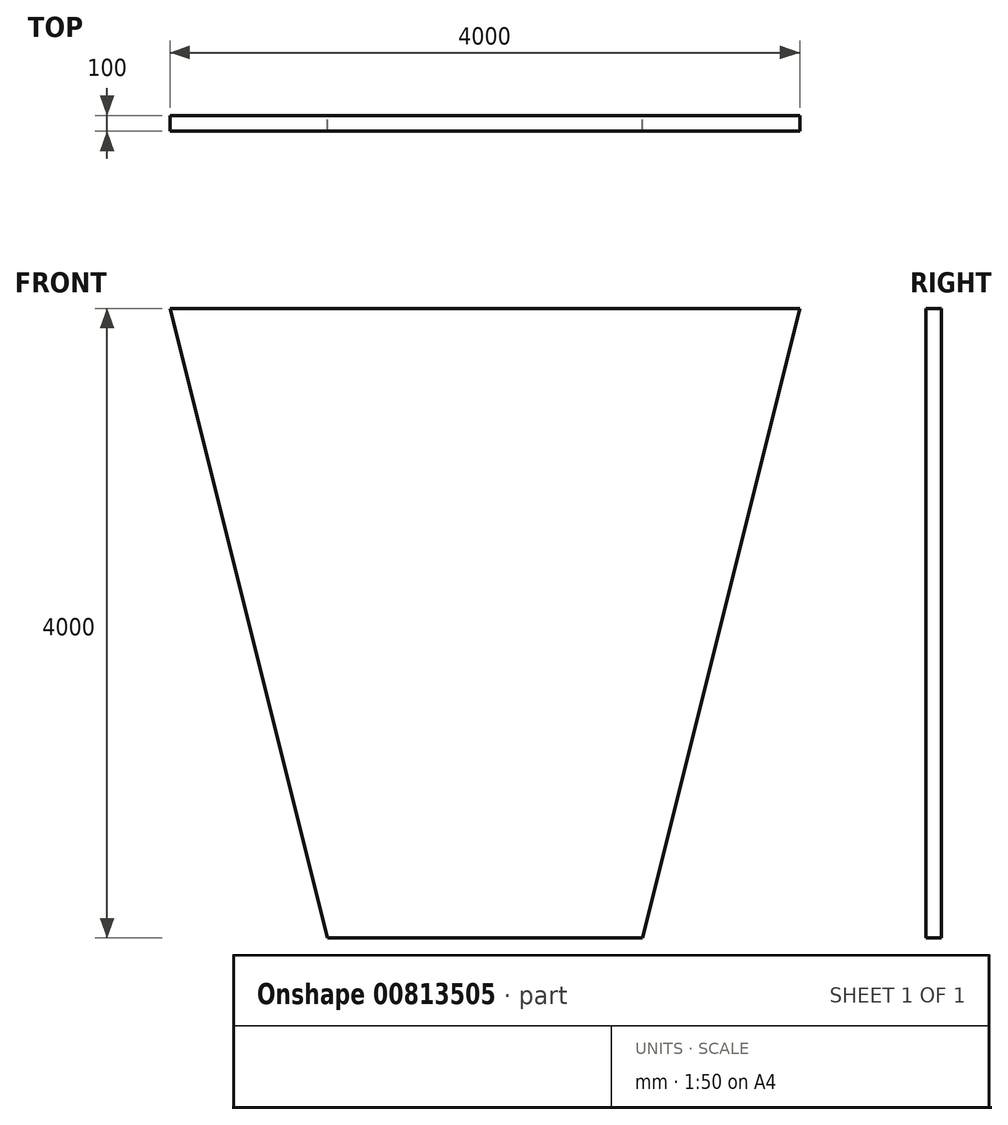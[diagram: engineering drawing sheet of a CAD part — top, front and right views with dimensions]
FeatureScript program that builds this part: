
annotation { "Feature Type Name" : "Feature", "Feature Type Description" : "" }
export const myFeature = defineFeature(function(context is Context, id is Id, definition is map)
    precondition{}
    {
        {
            var Q0;
            Q0=qCreatedBy(makeId("Front.planeOp"),FACE);
            var sketch = newSketch(context, id + "F0", { "sketchPlane" : qUnion([Q0])});
            skLineSegment(sketch, "E0", {"start": v(-2000, 3982.87) * mm, "end": v(0, 3982.87) * mm});
            skLineSegment(sketch, "E1.MirrorCS", {"start": v(2000, 3982.87) * mm, "end": v(0, 3982.87) * mm});
            skLineSegment(sketch, "E2", {"start": v(-1000, -17.13) * mm, "end": v(0, -17.13) * mm});
            skLineSegment(sketch, "E3.MirrorCS", {"start": v(1000, -17.13) * mm, "end": v(0, -17.13) * mm});
            skLineSegment(sketch, "E4", {"start": v(-2000, 3982.87) * mm, "end": v(-1000, -17.13) * mm});
            skLineSegment(sketch, "E5.MirrorCS", {"start": v(2000, 3982.87) * mm, "end": v(1000, -17.13) * mm});
            skSolve(sketch);
        }
        {
            var Q0;
            Q0=makeQuery(id+"F0.imprint","IMPRINT",FACE,{"disambiguationData":[TD([[makeQuery(id+"F0.imprint","IMPRINT",EDGE,{"derivedFrom":sQuery(id+"F0.wireOp",EDGE,"E0")}),-1.0]])]});
            extrude(context, id + "F1", {"entities" : qUnion([Q0]), "depth" : 100 * mm, "offsetDistance" : 25 * mm});
        }
    });
